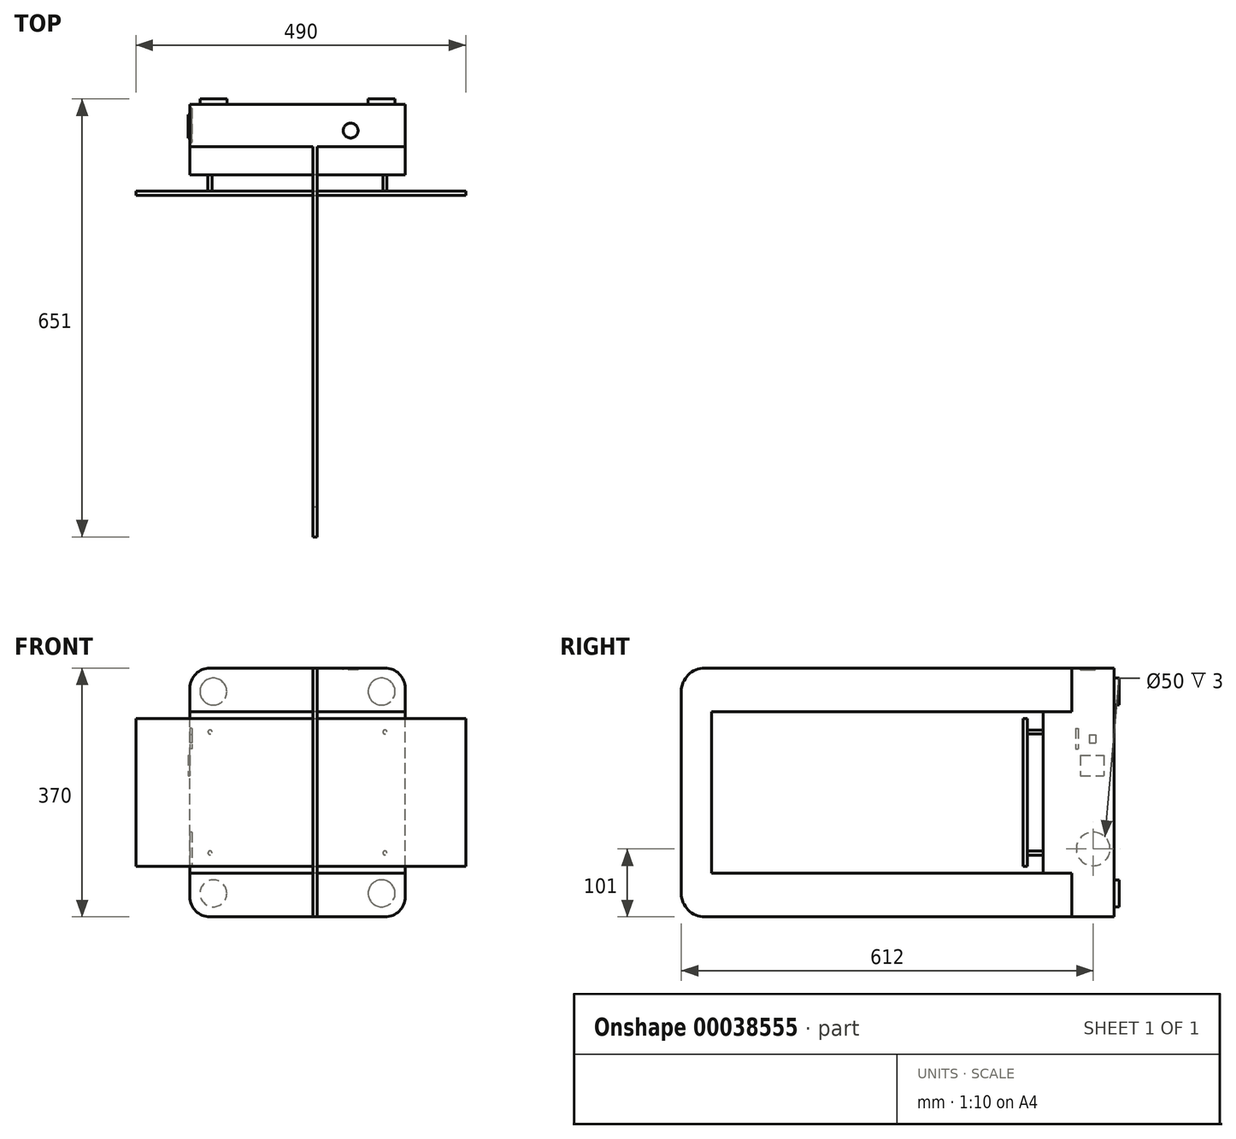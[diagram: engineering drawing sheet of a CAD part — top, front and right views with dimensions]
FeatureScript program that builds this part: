
annotation { "Feature Type Name" : "Feature", "Feature Type Description" : "" }
export const myFeature = defineFeature(function(context is Context, id is Id, definition is map)
    precondition{}
    {
        {
            var Q0;
            Q0=qCreatedBy(makeId("Front.planeOp"),FACE);
            var sketch = newSketch(context, id + "F0", { "sketchPlane" : qUnion([Q0])});
            skLineSegment(sketch, "E0.bottom", {"start": v(0, 0) * mm, "end": v(320, 0) * mm});
            skLineSegment(sketch, "E0.top", {"start": v(0, 370) * mm, "end": v(320, 370) * mm});
            skLineSegment(sketch, "E0.left", {"start": v(0, 0) * mm, "end": v(0, 370) * mm});
            skLineSegment(sketch, "E0.right", {"start": v(320, 0) * mm, "end": v(320, 370) * mm});
            skLineSegment(sketch, "E1", {"start": v(189, 0) * mm, "end": v(189, 370) * mm, "construction": true});
            skSolve(sketch);
        }
        {
            var Q0;
            Q0=makeQuery(id+"F0.imprint","IMPRINT",FACE,{"disambiguationData":[TD([[makeQuery(id+"F0.imprint","IMPRINT",EDGE,{"derivedFrom":sQuery(id+"F0.wireOp",EDGE,"E0.bottom")}),1.0]])]});
            extrude(context, id + "F1", {"entities" : qUnion([Q0]), "oppositeDirection" : true, "depth" : 63 * mm});
        }
        {
            var Q0;
            Q0=makeQuery(id+"F1.opExtrude","CAP_FACE",FACE,{"disambiguationData":[OSD([sQuery(id+"F0.wireOp",EDGE,"E0.bottom"),sQuery(id+"F0.wireOp",EDGE,"E0.top"),sQuery(id+"F0.wireOp",EDGE,"E0.left"),sQuery(id+"F0.wireOp",EDGE,"E0.right")])],"isStart":false});
            var sketch = newSketch(context, id + "F2", { "sketchPlane" : qUnion([Q0])});
            skCircle(sketch, "E2", {"center": v(-35, 35) * mm, "radius": 20 * mm});
            skCircle(sketch, "E3", {"center": v(-35, 335) * mm, "radius": 20 * mm});
            skCircle(sketch, "E4", {"center": v(-285, 335) * mm, "radius": 20 * mm});
            skCircle(sketch, "E5", {"center": v(-285, 35) * mm, "radius": 20 * mm});
            skLineSegment(sketch, "E6", {"start": v(-35, 370) * mm, "end": v(-35, 0) * mm, "construction": true});
            skLineSegment(sketch, "E7", {"start": v(-285, 370) * mm, "end": v(-285, 0) * mm, "construction": true});
            skLineSegment(sketch, "E8", {"start": v(0, 35) * mm, "end": v(-320, 35) * mm, "construction": true});
            skLineSegment(sketch, "E9", {"start": v(0, 335) * mm, "end": v(-320, 335) * mm, "construction": true});
            skSolve(sketch);
        }
        {
            var Q0;
            Q0=makeQuery(id+"F2.imprint","IMPRINT",FACE,{"disambiguationData":[TD([[makeQuery(id+"F2.imprint","IMPRINT",EDGE,{"derivedFrom":sQuery(id+"F2.wireOp",EDGE,"E5")}),1.0]])]});
            var Q1;
            Q1=makeQuery(id+"F2.imprint","IMPRINT",FACE,{"disambiguationData":[TD([[makeQuery(id+"F2.imprint","IMPRINT",EDGE,{"derivedFrom":sQuery(id+"F2.wireOp",EDGE,"E4")}),1.0]])]});
            var Q2;
            Q2=makeQuery(id+"F2.imprint","IMPRINT",FACE,{"disambiguationData":[TD([[makeQuery(id+"F2.imprint","IMPRINT",EDGE,{"derivedFrom":sQuery(id+"F2.wireOp",EDGE,"E3")}),1.0]])]});
            var Q3;
            Q3=makeQuery(id+"F2.imprint","IMPRINT",FACE,{"disambiguationData":[TD([[makeQuery(id+"F2.imprint","IMPRINT",EDGE,{"derivedFrom":sQuery(id+"F2.wireOp",EDGE,"E2")}),1.0]])]});
            extrude(context, id + "F3", {"entities" : qUnion([Q0, Q1, Q2, Q3]), "operationType" : NewBodyOperationType.ADD, "depth" : 8 * mm});
        }
        {
            var Q0;
            Q0=makeQuery(id+"F1.opExtrude","SWEPT_EDGE",EDGE,{"disambiguationData":[OSD([sQuery(id+"F0.wireOp",EDGE,"E0.bottom"),sQuery(id+"F0.wireOp",EDGE,"E0.left")])]});
            var Q1;
            Q1=makeQuery(id+"F1.opExtrude","SWEPT_EDGE",EDGE,{"disambiguationData":[OSD([sQuery(id+"F0.wireOp",EDGE,"E0.bottom"),sQuery(id+"F0.wireOp",EDGE,"E0.right")])]});
            var Q2;
            Q2=makeQuery(id+"F1.opExtrude","SWEPT_EDGE",EDGE,{"disambiguationData":[OSD([sQuery(id+"F0.wireOp",EDGE,"E0.top"),sQuery(id+"F0.wireOp",EDGE,"E0.right")])]});
            var Q3;
            Q3=makeQuery(id+"F1.opExtrude","SWEPT_EDGE",EDGE,{"disambiguationData":[OSD([sQuery(id+"F0.wireOp",EDGE,"E0.top"),sQuery(id+"F0.wireOp",EDGE,"E0.left")])]});
            fillet(context, id + "F4", {"entities" : qUnion([Q0, Q1, Q2, Q3]), "radius" : 30 * mm, "tangentPropagation" : true, "allowEdgeOverflow" : false});
        }
        {
            var Q0;
            Q0=sQuery(id+"F0.wireOp",EDGE,"E1");
            cPlane(context, id + "F5", {"entities" : qUnion([Q0]), "cplaneType" : CPlaneType.LINE_ANGLE, "offset" : 150 * mm, "angle" : 0 * degree, "width" : 150 * mm, "height" : 150 * mm});
        }
        {
            var Q0;
            Q0=qCreatedBy(id+"F5.planeOp",FACE);
            var sketch = newSketch(context, id + "F6", { "sketchPlane" : qUnion([Q0])});
            skLineSegment(sketch, "E10.bottom", {"start": v(0, 0) * mm, "end": v(-580, 0) * mm});
            skLineSegment(sketch, "E10.top", {"start": v(0, 370) * mm, "end": v(-580, 370) * mm});
            skLineSegment(sketch, "E10.left", {"start": v(0, 0) * mm, "end": v(0, 370) * mm});
            skLineSegment(sketch, "E10.right", {"start": v(-580, 0) * mm, "end": v(-580, 370) * mm});
            skSolve(sketch);
        }
        {
            var Q0;
            Q0=makeQuery(id+"F6.imprint","IMPRINT",FACE,{"disambiguationData":[TD([[makeQuery(id+"F6.imprint","IMPRINT",EDGE,{"derivedFrom":sQuery(id+"F6.wireOp",EDGE,"E10.bottom")}),-1.0]])]});
            extrude(context, id + "F7", {"entities" : qUnion([Q0]), "operationType" : NewBodyOperationType.ADD, "oppositeDirection" : true, "depth" : 6 * mm});
        }
        {
            var Q0;
            Q0=makeQuery(id+"F7.opExtrude","CAP_FACE",FACE,{"disambiguationData":[OSD([sQuery(id+"F6.wireOp",EDGE,"E10.bottom"),sQuery(id+"F6.wireOp",EDGE,"E10.top"),sQuery(id+"F6.wireOp",EDGE,"E10.left"),sQuery(id+"F6.wireOp",EDGE,"E10.right")])],"isStart":true});
            var sketch = newSketch(context, id + "F8", { "sketchPlane" : qUnion([Q0])});
            skLineSegment(sketch, "E11.bottom", {"start": v(0, 65) * mm, "end": v(-535, 65) * mm});
            skLineSegment(sketch, "E11.top", {"start": v(0, 305) * mm, "end": v(-535, 305) * mm});
            skLineSegment(sketch, "E11.left", {"start": v(0, 65) * mm, "end": v(0, 305) * mm});
            skLineSegment(sketch, "E11.right", {"start": v(-535, 65) * mm, "end": v(-535, 305) * mm});
            skSolve(sketch);
        }
        {
            var Q0;
            Q0=makeQuery(id+"F8.imprint","IMPRINT",FACE,{"disambiguationData":[TD([[makeQuery(id+"F8.imprint","IMPRINT",EDGE,{"derivedFrom":sQuery(id+"F8.wireOp",EDGE,"E11.bottom")}),-1.0]])]});
            extrude(context, id + "F9", {"entities" : qUnion([Q0]), "operationType" : NewBodyOperationType.REMOVE, "endBound" : BoundingType.THROUGH_ALL, "oppositeDirection" : true, "depth" : 25 * mm});
        }
        {
            var Q0;
            Q0=makeQuery(id+"F7.opExtrude","SWEPT_EDGE",EDGE,{"disambiguationData":[OSD([sQuery(id+"F6.wireOp",EDGE,"E10.bottom"),sQuery(id+"F6.wireOp",EDGE,"E10.right")])]});
            var Q1;
            Q1=makeQuery(id+"F7.opExtrude","SWEPT_EDGE",EDGE,{"disambiguationData":[OSD([sQuery(id+"F6.wireOp",EDGE,"E10.top"),sQuery(id+"F6.wireOp",EDGE,"E10.right")])]});
            fillet(context, id + "F10", {"entities" : qUnion([Q0, Q1]), "radius" : 35 * mm, "tangentPropagation" : true, "allowEdgeOverflow" : false});
        }
        {
            var Q0;
            Q0=makeQuery(id+"F0.imprint","IMPRINT",FACE,{"disambiguationData":[TD([[makeQuery(id+"F0.imprint","IMPRINT",EDGE,{"derivedFrom":sQuery(id+"F0.wireOp",EDGE,"E0.bottom")}),1.0]])]});
            var sketch = newSketch(context, id + "F11", { "sketchPlane" : qUnion([Q0])});
            skLineSegment(sketch, "E12.bottom", {"start": v(320, 65) * mm, "end": v(0, 65) * mm});
            skLineSegment(sketch, "E12.top", {"start": v(320, 305) * mm, "end": v(0, 305) * mm});
            skLineSegment(sketch, "E12.left", {"start": v(320, 65) * mm, "end": v(320, 305) * mm});
            skLineSegment(sketch, "E12.right", {"start": v(0, 65) * mm, "end": v(0, 305) * mm});
            skSolve(sketch);
        }
        {
            var Q0;
            Q0=makeQuery(id+"F11.imprint","IMPRINT",FACE,{"disambiguationData":[TD([[makeQuery(id+"F11.imprint","IMPRINT",EDGE,{"derivedFrom":sQuery(id+"F11.wireOp",EDGE,"E12.bottom")}),-1.0]])]});
            extrude(context, id + "F12", {"entities" : qUnion([Q0]), "operationType" : NewBodyOperationType.ADD, "depth" : 42 * mm});
        }
        {
            var Q0;
            Q0=makeQuery(id+"F7.boolean.opBoolean","MERGE",FACE,{"derivedFrom":[makeQuery(id+"F1.opExtrude","SWEPT_FACE",FACE,{"disambiguationData":[OSD([sQuery(id+"F0.wireOp",EDGE,"E0.top")])]}),makeQuery(id+"F7.opExtrude","SWEPT_FACE",FACE,{"disambiguationData":[OSD([sQuery(id+"F6.wireOp",EDGE,"E10.top")])]})]});
            var sketch = newSketch(context, id + "F13", { "sketchPlane" : qUnion([Q0])});
            skCircle(sketch, "E13", {"center": v(239, 24) * mm, "radius": 11 * mm});
            skSolve(sketch);
        }
        {
            var Q0;
            Q0=makeQuery(id+"F13.imprint","IMPRINT",FACE,{"disambiguationData":[TD([[makeQuery(id+"F13.imprint","IMPRINT",EDGE,{"derivedFrom":sQuery(id+"F13.wireOp",EDGE,"E13")}),1.0]])]});
            extrude(context, id + "F14", {"entities" : qUnion([Q0]), "operationType" : NewBodyOperationType.REMOVE, "oppositeDirection" : true, "depth" : 3 * mm});
        }
        {
            var Q0;
            Q0=makeQuery(id+"F12.boolean.opBoolean","MERGE",FACE,{"derivedFrom":[makeQuery(id+"F1.opExtrude","SWEPT_FACE",FACE,{"disambiguationData":[OSD([sQuery(id+"F0.wireOp",EDGE,"E0.left")])]}),makeQuery(id+"F12.opExtrude","SWEPT_FACE",FACE,{"disambiguationData":[OSD([sQuery(id+"F11.wireOp",EDGE,"E12.right")])]})]});
            var sketch = newSketch(context, id + "F15", { "sketchPlane" : qUnion([Q0])});
            skLineSegment(sketch, "E14.bottom", {"start": v(-6, 280) * mm, "end": v(-10, 280) * mm});
            skLineSegment(sketch, "E14.top", {"start": v(-6, 250) * mm, "end": v(-10, 250) * mm});
            skLineSegment(sketch, "E14.left", {"start": v(-6, 280) * mm, "end": v(-6, 250) * mm});
            skLineSegment(sketch, "E14.right", {"start": v(-10, 280) * mm, "end": v(-10, 250) * mm});
            skLineSegment(sketch, "E15.bottom", {"start": v(-13, 240) * mm, "end": v(-48, 240) * mm});
            skLineSegment(sketch, "E15.top", {"start": v(-13, 210) * mm, "end": v(-48, 210) * mm});
            skLineSegment(sketch, "E15.left", {"start": v(-13, 240) * mm, "end": v(-13, 210) * mm});
            skLineSegment(sketch, "E15.right", {"start": v(-48, 240) * mm, "end": v(-48, 210) * mm});
            skLineSegment(sketch, "E16.bottom", {"start": v(-26, 271) * mm, "end": v(-36, 271) * mm});
            skLineSegment(sketch, "E16.top", {"start": v(-26, 259) * mm, "end": v(-36, 259) * mm});
            skLineSegment(sketch, "E16.left", {"start": v(-26, 271) * mm, "end": v(-26, 259) * mm});
            skLineSegment(sketch, "E16.right", {"start": v(-36, 271) * mm, "end": v(-36, 259) * mm});
            skCircle(sketch, "E17", {"center": v(-32, 101) * mm, "radius": 25 * mm});
            skLineSegment(sketch, "E18", {"start": v(-10, 265) * mm, "end": v(-63, 265) * mm, "construction": true});
            skSolve(sketch);
        }
        {
            var Q0;
            Q0=makeQuery(id+"F15.imprint","IMPRINT",FACE,{"disambiguationData":[TD([[makeQuery(id+"F15.imprint","IMPRINT",EDGE,{"derivedFrom":sQuery(id+"F15.wireOp",EDGE,"E17")}),1.0]])]});
            var Q1;
            Q1=makeQuery(id+"F15.imprint","IMPRINT",FACE,{"disambiguationData":[TD([[makeQuery(id+"F15.imprint","IMPRINT",EDGE,{"derivedFrom":sQuery(id+"F15.wireOp",EDGE,"E14.bottom")}),1.0]])]});
            var Q2;
            Q2=makeQuery(id+"F15.imprint","IMPRINT",FACE,{"disambiguationData":[TD([[makeQuery(id+"F15.imprint","IMPRINT",EDGE,{"derivedFrom":sQuery(id+"F15.wireOp",EDGE,"E16.bottom")}),1.0]])]});
            extrude(context, id + "F16", {"entities" : qUnion([Q0, Q1, Q2]), "operationType" : NewBodyOperationType.REMOVE, "oppositeDirection" : true, "depth" : 3 * mm});
        }
        {
            var Q0;
            Q0=makeQuery(id+"F15.imprint","IMPRINT",FACE,{"disambiguationData":[TD([[makeQuery(id+"F15.imprint","IMPRINT",EDGE,{"derivedFrom":sQuery(id+"F15.wireOp",EDGE,"E15.bottom")}),1.0]])]});
            extrude(context, id + "F17", {"entities" : qUnion([Q0]), "operationType" : NewBodyOperationType.ADD, "depth" : 2.5 * mm});
        }
        {
            var Q0;
            Q0=makeQuery(id+"F12.opExtrude","CAP_FACE",FACE,{"disambiguationData":[OSD([sQuery(id+"F11.wireOp",EDGE,"E12.bottom"),sQuery(id+"F11.wireOp",EDGE,"E12.top"),sQuery(id+"F11.wireOp",EDGE,"E12.left"),sQuery(id+"F11.wireOp",EDGE,"E12.right")])],"isStart":false});
            var sketch = newSketch(context, id + "F18", { "sketchPlane" : qUnion([Q0])});
            skCircle(sketch, "E19", {"center": v(30, 95) * mm, "radius": 3 * mm});
            skCircle(sketch, "E20", {"center": v(30, 275) * mm, "radius": 3 * mm});
            skCircle(sketch, "E21", {"center": v(290, 95) * mm, "radius": 3 * mm});
            skCircle(sketch, "E22", {"center": v(290, 275) * mm, "radius": 3 * mm});
            skLineSegment(sketch, "E23", {"start": v(320, 95) * mm, "end": v(0, 95) * mm, "construction": true});
            skLineSegment(sketch, "E24", {"start": v(290, 65) * mm, "end": v(290, 305) * mm, "construction": true});
            skLineSegment(sketch, "E25", {"start": v(320, 275) * mm, "end": v(0, 275) * mm, "construction": true});
            skLineSegment(sketch, "E26", {"start": v(30, 65) * mm, "end": v(30, 305) * mm, "construction": true});
            skSolve(sketch);
        }
        {
            var Q0;
            Q0=makeQuery(id+"F18.imprint","IMPRINT",FACE,{"disambiguationData":[TD([[makeQuery(id+"F18.imprint","IMPRINT",EDGE,{"derivedFrom":sQuery(id+"F18.wireOp",EDGE,"E19")}),1.0]])]});
            var Q1;
            Q1=makeQuery(id+"F18.imprint","IMPRINT",FACE,{"disambiguationData":[TD([[makeQuery(id+"F18.imprint","IMPRINT",EDGE,{"derivedFrom":sQuery(id+"F18.wireOp",EDGE,"E20")}),1.0]])]});
            var Q2;
            Q2=makeQuery(id+"F18.imprint","IMPRINT",FACE,{"disambiguationData":[TD([[makeQuery(id+"F18.imprint","IMPRINT",EDGE,{"derivedFrom":sQuery(id+"F18.wireOp",EDGE,"E21")}),1.0]])]});
            var Q3;
            Q3=makeQuery(id+"F18.imprint","IMPRINT",FACE,{"disambiguationData":[TD([[makeQuery(id+"F18.imprint","IMPRINT",EDGE,{"derivedFrom":sQuery(id+"F18.wireOp",EDGE,"E22")}),1.0]])]});
            extrude(context, id + "F19", {"entities" : qUnion([Q0, Q1, Q2, Q3]), "operationType" : NewBodyOperationType.ADD, "depth" : 24 * mm});
        }
        {
            var Q0;
            Q0=makeQuery(id+"F12.opExtrude","CAP_FACE",FACE,{"disambiguationData":[OSD([sQuery(id+"F11.wireOp",EDGE,"E12.bottom"),sQuery(id+"F11.wireOp",EDGE,"E12.top"),sQuery(id+"F11.wireOp",EDGE,"E12.left"),sQuery(id+"F11.wireOp",EDGE,"E12.right")])],"isStart":false});
            cPlane(context, id + "F20", {"entities" : qUnion([Q0]), "cplaneType" : CPlaneType.OFFSET, "offset" : 24 * mm, "width" : 150 * mm, "height" : 150 * mm});
        }
        {
            var Q0;
            Q0=qCreatedBy(id+"F20.planeOp",FACE);
            var sketch = newSketch(context, id + "F21", { "sketchPlane" : qUnion([Q0])});
            skLineSegment(sketch, "E27.bottom", {"start": v(-80, 75) * mm, "end": v(410, 75) * mm});
            skLineSegment(sketch, "E27.top", {"start": v(-80, 295) * mm, "end": v(410, 295) * mm});
            skLineSegment(sketch, "E27.left", {"start": v(-80, 75) * mm, "end": v(-80, 295) * mm});
            skLineSegment(sketch, "E27.right", {"start": v(410, 75) * mm, "end": v(410, 295) * mm});
            skSolve(sketch);
        }
        {
            var Q0;
            Q0=makeQuery(id+"F21.imprint","IMPRINT",FACE,{"disambiguationData":[TD([[makeQuery(id+"F21.imprint","IMPRINT",EDGE,{"derivedFrom":sQuery(id+"F21.wireOp",EDGE,"E27.bottom")}),1.0]])]});
            extrude(context, id + "F22", {"entities" : qUnion([Q0]), "operationType" : NewBodyOperationType.ADD, "depth" : 6 * mm});
        }
    });
